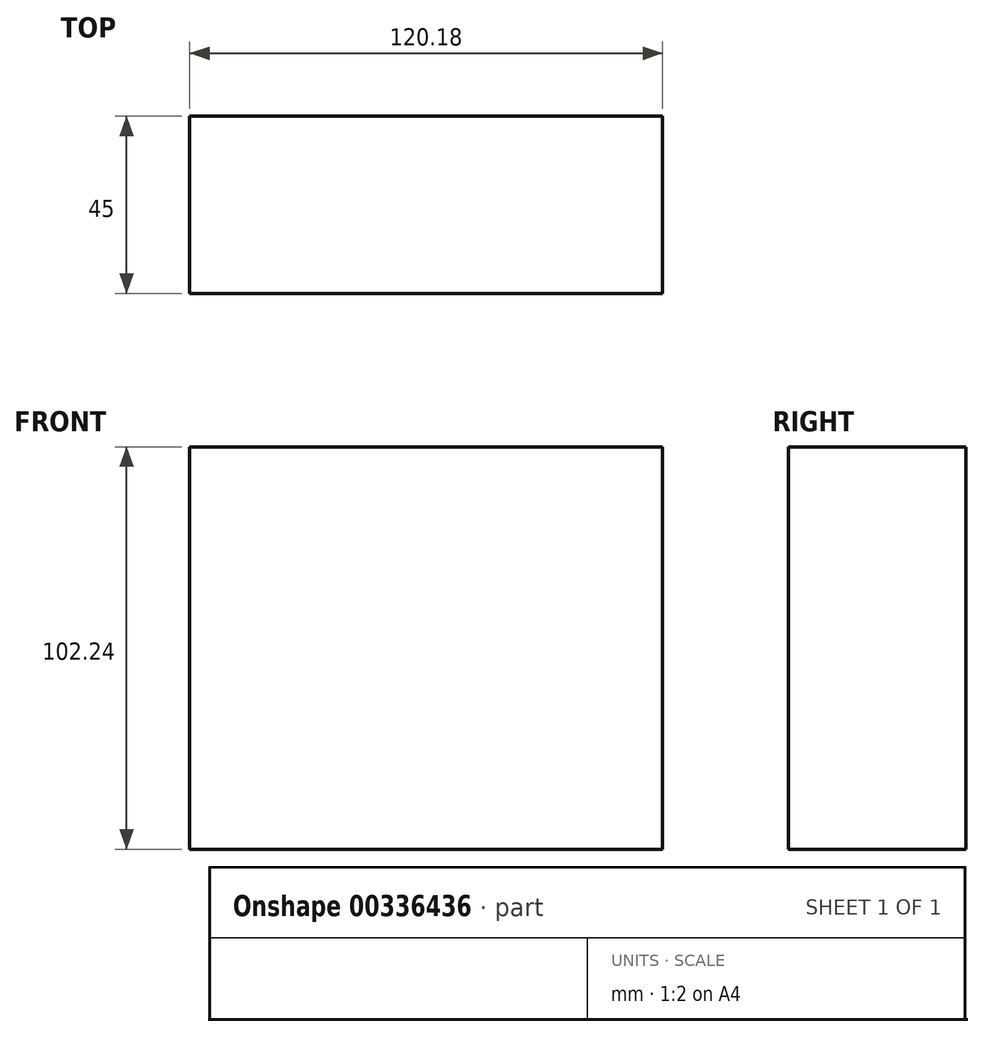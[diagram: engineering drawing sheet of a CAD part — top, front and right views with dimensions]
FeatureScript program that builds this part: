
annotation { "Feature Type Name" : "Feature", "Feature Type Description" : "" }
export const myFeature = defineFeature(function(context is Context, id is Id, definition is map)
    precondition{}
    {
        {
            var Q0;
            Q0=qCreatedBy(makeId("Front.planeOp"),FACE);
            var sketch = newSketch(context, id + "F0", { "sketchPlane" : qUnion([Q0])});
            skLineSegment(sketch, "E0.bottom", {"start": v(60.09, 51.12) * mm, "end": v(-60.09, 51.12) * mm});
            skLineSegment(sketch, "E0.top", {"start": v(60.09, -51.12) * mm, "end": v(-60.09, -51.12) * mm});
            skLineSegment(sketch, "E0.left", {"start": v(60.09, 51.12) * mm, "end": v(60.09, -51.12) * mm});
            skLineSegment(sketch, "E0.right", {"start": v(-60.09, 51.12) * mm, "end": v(-60.09, -51.12) * mm});
            skPoint(sketch, "E0.middle", {"position": v(0, 0) * mm});
            skSolve(sketch);
        }
        {
            var Q0;
            Q0=makeQuery(id+"F0.imprint","IMPRINT",FACE,{"disambiguationData":[TD([[makeQuery(id+"F0.imprint","IMPRINT",EDGE,{"derivedFrom":sQuery(id+"F0.wireOp",EDGE,"E0.bottom")}),1.0]])]});
            extrude(context, id + "F1", {"entities" : qUnion([Q0]), "depth" : 20 * mm});
        }
        {
            var Q0;
            Q0=makeQuery(id+"F1.opExtrude","CAP_FACE",FACE,{"disambiguationData":[OSD([sQuery(id+"F0.wireOp",EDGE,"E0.bottom"),sQuery(id+"F0.wireOp",EDGE,"E0.top"),sQuery(id+"F0.wireOp",EDGE,"E0.left"),sQuery(id+"F0.wireOp",EDGE,"E0.right")])],"isStart":false});
            var sketch = newSketch(context, id + "F2", { "sketchPlane" : qUnion([Q0])});
            skSolve(sketch);
        }
        {
            var Q0;
            Q0=makeQuery(id+"F2.imprint","IMPRINT",FACE,{"disambiguationData":[TD([[makeQuery(id+"F2.imprint","IMPRINT",EDGE,{"derivedFrom":makeQuery(id+"F1.opExtrude","CAP_EDGE",EDGE,{"disambiguationData":[OSD([sQuery(id+"F0.wireOp",EDGE,"E0.bottom")])],"isStart":false})}),1.0]])]});
            extrude(context, id + "F3", {"entities" : qUnion([Q0]), "operationType" : NewBodyOperationType.ADD, "depth" : 25 * mm});
        }
    });
